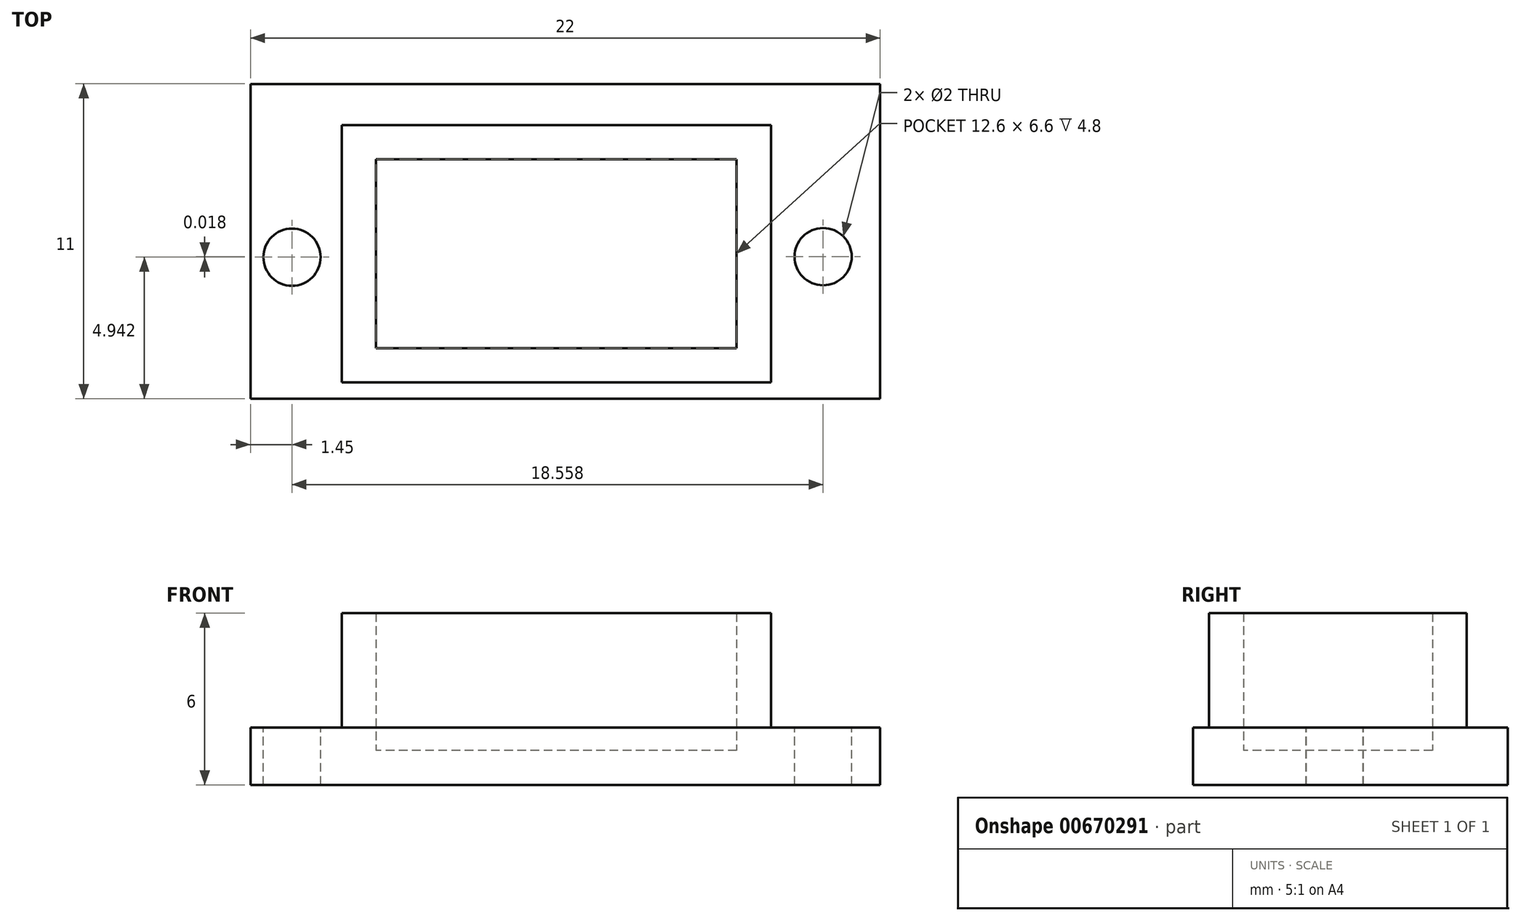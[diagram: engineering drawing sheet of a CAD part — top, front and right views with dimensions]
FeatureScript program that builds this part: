
annotation { "Feature Type Name" : "Feature", "Feature Type Description" : "" }
export const myFeature = defineFeature(function(context is Context, id is Id, definition is map)
    precondition{}
    {
        {
            var Q0;
            Q0=qCreatedBy(makeId("Top.planeOp"),FACE);
            var sketch = newSketch(context, id + "F0", { "sketchPlane" : qUnion([Q0])});
            skLineSegment(sketch, "E0.bottom", {"start": v(-0.42, 6.04) * mm, "end": v(21.58, 6.04) * mm});
            skLineSegment(sketch, "E0.top", {"start": v(-0.42, -4.96) * mm, "end": v(21.58, -4.96) * mm});
            skLineSegment(sketch, "E0.left", {"start": v(-0.42, 6.04) * mm, "end": v(-0.42, -4.96) * mm});
            skLineSegment(sketch, "E0.right", {"start": v(21.58, 6.04) * mm, "end": v(21.58, -4.96) * mm});
            skSolve(sketch);
        }
        {
            var Q0;
            Q0=makeQuery(id+"F0.imprint","IMPRINT",FACE,{"disambiguationData":[TD([[makeQuery(id+"F0.imprint","IMPRINT",EDGE,{"derivedFrom":sQuery(id+"F0.wireOp",EDGE,"E0.bottom")}),-1.0]])]});
            extrude(context, id + "F1", {"entities" : qUnion([Q0]), "depth" : 2 * mm, "offsetDistance" : 25 * mm});
        }
        {
            var Q0;
            Q0=qCreatedBy(makeId("Top.planeOp"),FACE);
            var sketch = newSketch(context, id + "F2", { "sketchPlane" : qUnion([Q0])});
            skLineSegment(sketch, "E1.bottom", {"start": v(2.77, -4.4) * mm, "end": v(17.77, -4.4) * mm});
            skLineSegment(sketch, "E1.top", {"start": v(2.77, 4.6) * mm, "end": v(17.77, 4.6) * mm});
            skLineSegment(sketch, "E1.left", {"start": v(2.77, -4.4) * mm, "end": v(2.77, 4.6) * mm});
            skLineSegment(sketch, "E1.right", {"start": v(17.77, -4.4) * mm, "end": v(17.77, 4.6) * mm});
            skSolve(sketch);
        }
        {
            var Q0;
            Q0=qSketchRegion(id+"F2",true);
            extrude(context, id + "F3", {"entities" : qUnion([Q0]), "operationType" : NewBodyOperationType.ADD, "depth" : 6 * mm, "offsetDistance" : 25 * mm});
        }
        {
            var Q0;
            Q0=makeQuery(id+"F3.opExtrude","CAP_FACE",FACE,{"disambiguationData":[OSD([sQuery(id+"F2.wireOp",EDGE,"E1.bottom"),sQuery(id+"F2.wireOp",EDGE,"E1.top"),sQuery(id+"F2.wireOp",EDGE,"E1.left"),sQuery(id+"F2.wireOp",EDGE,"E1.right")])],"isStart":false});
            shell(context, id + "F4", {"entities" : qUnion([Q0]), "thickness" : 1.2 * mm});
        }
        {
            var Q0;
            Q0=makeQuery(id+"F1.opExtrude","CAP_FACE",FACE,{"disambiguationData":[OSD([sQuery(id+"F0.wireOp",EDGE,"E0.bottom"),sQuery(id+"F0.wireOp",EDGE,"E0.top"),sQuery(id+"F0.wireOp",EDGE,"E0.left"),sQuery(id+"F0.wireOp",EDGE,"E0.right")])],"isStart":false});
            var sketch = newSketch(context, id + "F5", { "sketchPlane" : qUnion([Q0])});
            skCircle(sketch, "E2", {"center": v(1.03, -0.02) * mm, "radius": 1 * mm});
            skSolve(sketch);
        }
        {
            var Q0;
            {var subQ0=makeQuery(id+"F1.opExtrude","CAP_FACE",FACE,{"disambiguationData":[OSD([sQuery(id+"F0.wireOp",EDGE,"E0.bottom"),sQuery(id+"F0.wireOp",EDGE,"E0.top"),sQuery(id+"F0.wireOp",EDGE,"E0.left"),sQuery(id+"F0.wireOp",EDGE,"E0.right")])],"isStart":false});Q0=makeQuery(id+"F5.imprint","IMPRINT",FACE,{"disambiguationData":[TD([[makeQuery(id+"F5.imprint","IMPRINT",EDGE,{"derivedFrom":makeQuery(id+"F3.boolean.opBoolean","INTERSECT",EDGE,{"derivedFrom":[subQ0,makeQuery(id+"F3.opExtrude","SWEPT_FACE",FACE,{"disambiguationData":[OSD([sQuery(id+"F2.wireOp",EDGE,"E1.bottom")])]})]})}),-1.0]])]});}
            var sketch = newSketch(context, id + "F6", { "sketchPlane" : qUnion([Q0])});
            skCircle(sketch, "E3", {"center": v(19.59, 0) * mm, "radius": 1 * mm});
            skSolve(sketch);
        }
        {
            var Q0;
            Q0=qSketchRegion(id+"F6",true);
            extrude(context, id + "F7", {"entities" : qUnion([Q0]), "operationType" : NewBodyOperationType.REMOVE, "oppositeDirection" : true, "depth" : 25 * mm, "offsetDistance" : 25 * mm});
        }
        {
            var Q0;
            Q0=qSketchRegion(id+"F5",true);
            extrude(context, id + "F8", {"entities" : qUnion([Q0]), "operationType" : NewBodyOperationType.REMOVE, "oppositeDirection" : true, "depth" : 25 * mm, "offsetDistance" : 25 * mm});
        }
    });
